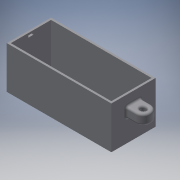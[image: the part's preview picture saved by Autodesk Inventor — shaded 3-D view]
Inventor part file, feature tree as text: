
AUTODESK INVENTOR PART (.ipt)
format: ipt  version: 2019 (Build 230136000, 136)  size: 196,608 bytes
history: native  units: mm
features: sketch x7, extrude x6, hole x1, fillet x1, projected_geometry x1
ambient origin geometry x8: Origin, YZ Plane, XZ Plane, XY Plane, X Axis, Y Axis, Z Axis, Center Point
bodies: Solid1 (feature_tree)
feature tree (16):
  extrude  "Extrusion1"  Depth=2.0mm
  extrude  "Extrusion2"  Depth=5.0mm
  extrude  "Extrusion3"  Depth=2.0mm
  extrude  "Extrusion4"  TaperAngle=0.0deg  [1 undecoded]
  extrude  "Extrusion5"  Depth=15.0mm
  hole  "Hole1"  [1 undecoded]
  fillet  "Fillet1"  Radius=10.0mm
  extrude  "Extrusion6"  Depth=2.0mm
  sketch  "Sketch1"  dims[d4=0.0mm d5=2.0mm]
  sketch  "Sketch2"  dims[d6=0.0mm d7=5.0mm]
  sketch  "Sketch3"  dims[d8=2.0mm d9=2.0mm]
  sketch  "Sketch4"  dims[d10=2.0mm d11=0.0mm]
  sketch  "Sketch5"  dims[d12=10.0mm d13=15.0mm]
  projected_geometry  "Projected Loop1"
  sketch  "Sketch6"  dims[d14=2.0mm d15=10.0mm d16=0.0mm d17=10.0mm d18=0.0mm]
  sketch  "Sketch7"  dims[d19=5.5mm d20=6.0mm d21=10.4mm d22=2.0mm d23=90.0deg d24=8.0mm d25=20.594885mm d26=2.0mm d27=8.0mm d28=3.0mm d29=0.0mm]
note: 2 required parameter values undecoded (feature->parameter linkage not recoverable at this tier; creation-order binding heuristic only, values carry confidence <= 0.55)
